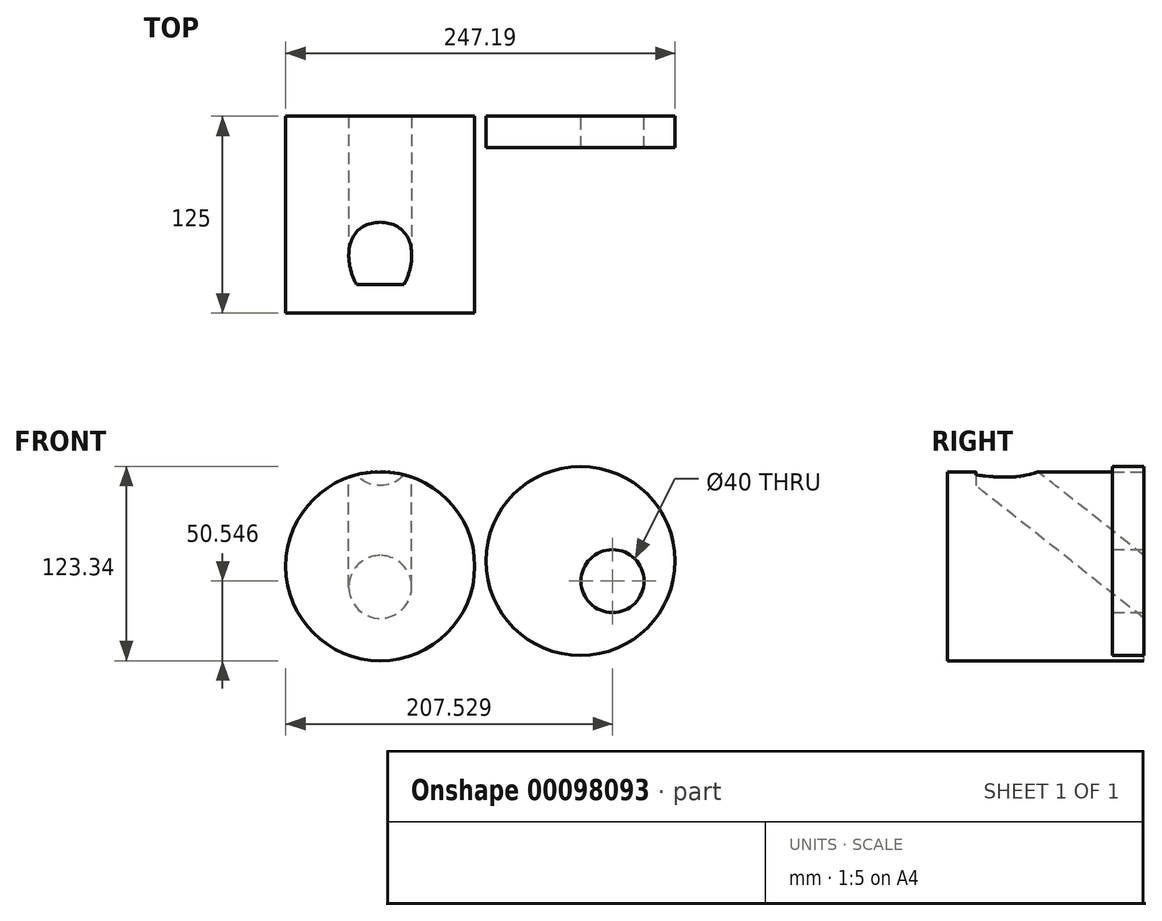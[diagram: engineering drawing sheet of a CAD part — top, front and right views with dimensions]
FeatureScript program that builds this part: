
annotation { "Feature Type Name" : "Feature", "Feature Type Description" : "" }
export const myFeature = defineFeature(function(context is Context, id is Id, definition is map)
    precondition{}
    {
        {
            var Q0;
            Q0=qCreatedBy(makeId("Front.planeOp"),FACE);
            var sketch = newSketch(context, id + "F0", { "sketchPlane" : qUnion([Q0])});
            skCircle(sketch, "E0", {"center": v(0, 0) * mm, "radius": 60 * mm});
            skSolve(sketch);
        }
        {
            var Q0;
            Q0 = qSketchRegion(id + "F0", true);
            extrude(context, id + "F1", {"entities" : qUnion([Q0]), "depth" : 125 * mm});
        }
        {
            var Q0;
            Q0=makeQuery(id+"F1.opExtrude","CAP_FACE",FACE,{"disambiguationData":[OSD([sQuery(id+"F0.wireOp",EDGE,"E0")])],"isStart":true});
            var sketch = newSketch(context, id + "F2", { "sketchPlane" : qUnion([Q0])});
            skCircle(sketch, "E1", {"center": v(0, -13.15) * mm, "radius": 20 * mm});
            skSolve(sketch);
        }
        {
            var Q0;
            Q0=qCreatedBy(makeId("Right.planeOp"),FACE);
            var sketch = newSketch(context, id + "F3", { "sketchPlane" : qUnion([Q0])});
            skLineSegment(sketch, "E2", {"start": v(0, -25.44) * mm, "end": v(-106.84, 58.9) * mm});
            skSolve(sketch);
        }
        {
            var Q0;
            Q0=makeQuery(id+"F2.imprint","IMPRINT",FACE,{"disambiguationData":[TD([[makeQuery(id+"F2.imprint","IMPRINT",EDGE,{"derivedFrom":sQuery(id+"F2.wireOp",EDGE,"E1")}),1.0]])]});
            var Q1;
            Q1=sQuery(id+"F3.wireOp",EDGE,"E2");
            sweep(context, id + "F4", {"operationType" : NewBodyOperationType.REMOVE, "profiles" : qUnion([Q0]), "path" : qUnion([Q1])});
        }
        {
            var Q0;
            Q0=qCreatedBy(makeId("Front.planeOp"),FACE);
            var sketch = newSketch(context, id + "F5", { "sketchPlane" : qUnion([Q0])});
            skCircle(sketch, "E3", {"center": v(127.2, 3.34) * mm, "radius": 60 * mm});
            skSolve(sketch);
        }
        {
            var Q0;
            Q0 = qSketchRegion(id + "F5", true);
            extrude(context, id + "F6", {"entities" : qUnion([Q0]), "depth" : 20 * mm});
        }
        {
            var Q0;
            Q0=makeQuery(id+"F6.opExtrude","CAP_FACE",FACE,{"disambiguationData":[OSD([sQuery(id+"F5.wireOp",EDGE,"E3")])],"isStart":true});
            var sketch = newSketch(context, id + "F7", { "sketchPlane" : qUnion([Q0])});
            skCircle(sketch, "E4", {"center": v(-147.53, -9.45) * mm, "radius": 20 * mm});
            skSolve(sketch);
        }
        {
            var Q0;
            Q0=makeQuery(id+"F7.imprint","IMPRINT",FACE,{"disambiguationData":[TD([[makeQuery(id+"F7.imprint","IMPRINT",EDGE,{"derivedFrom":sQuery(id+"F7.wireOp",EDGE,"E4")}),1.0]])]});
            extrude(context, id + "F8", {"entities" : qUnion([Q0]), "operationType" : NewBodyOperationType.REMOVE, "oppositeDirection" : true, "depth" : 30 * mm});
        }
    });
